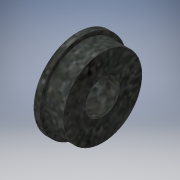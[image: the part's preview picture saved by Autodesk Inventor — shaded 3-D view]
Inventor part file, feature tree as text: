
AUTODESK INVENTOR PART (.ipt)
format: ipt  version: 2019 (Build 230136000, 136)  size: 223,232 bytes
history: native  units: in
note: dims shown in document units (in); Inventor stores cm internally (conversion verified against a paired STEP export)
features: revolve x1
ambient origin geometry x8: Origin, YZ Plane, XZ Plane, XY Plane, X Axis, Y Axis, Z Axis, Center Point
bodies: Solid1 (feature_tree)
feature tree (1):
  revolve  "Revolve1"  [1 undecoded]
note: 1 required parameter value undecoded (feature->parameter linkage not recoverable at this tier; creation-order binding heuristic only, values carry confidence <= 0.55)
